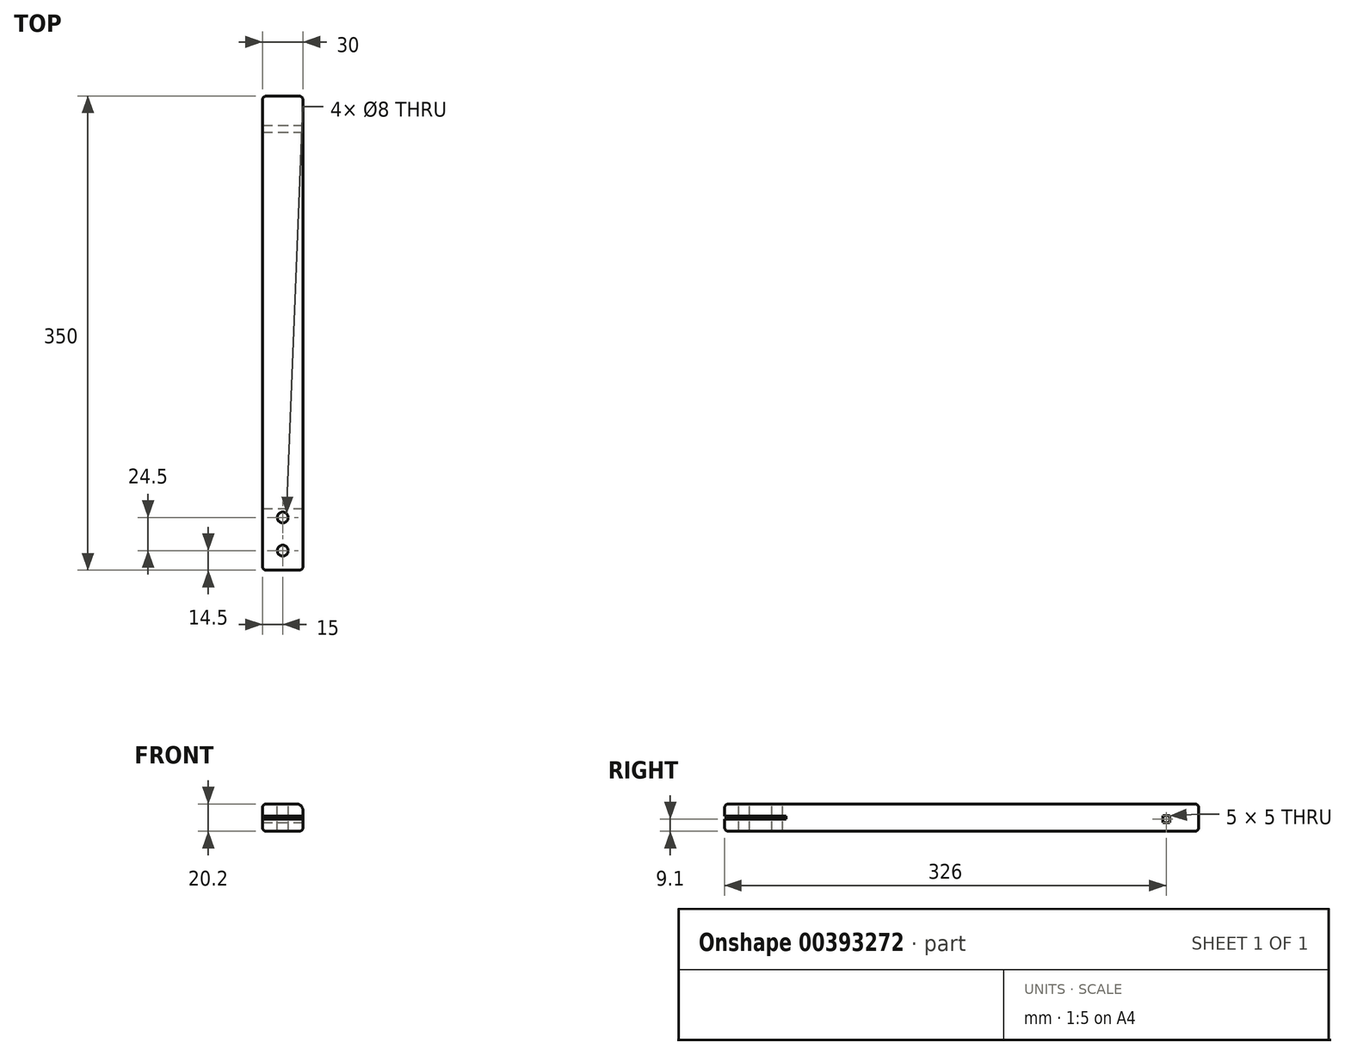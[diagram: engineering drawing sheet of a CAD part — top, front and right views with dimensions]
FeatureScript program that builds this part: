
annotation { "Feature Type Name" : "Feature", "Feature Type Description" : "" }
export const myFeature = defineFeature(function(context is Context, id is Id, definition is map)
    precondition{}
    {
        {
            var Q0;
            Q0=qCreatedBy(makeId("Front.planeOp"),FACE);
            var sketch = newSketch(context, id + "F0", { "sketchPlane" : qUnion([Q0])});
            skLineSegment(sketch, "E0.bottom", {"start": v(-15, -10.1) * mm, "end": v(15, -10.1) * mm});
            skLineSegment(sketch, "E0.top", {"start": v(-15, 10.1) * mm, "end": v(15, 10.1) * mm});
            skLineSegment(sketch, "E0.left", {"start": v(-15, -10.1) * mm, "end": v(-15, 10.1) * mm});
            skLineSegment(sketch, "E0.right", {"start": v(15, -10.1) * mm, "end": v(15, 10.1) * mm});
            skPoint(sketch, "E0.middle", {"position": v(0, 0) * mm});
            skSolve(sketch);
        }
        {
            var Q0;
            Q0 = qSketchRegion(id + "F0", true);
            extrude(context, id + "F1", {"entities" : qUnion([Q0]), "oppositeDirection" : true, "depth" : 350 * mm});
        }
        {
            var Q0;
            Q0=makeQuery(id+"F1.opExtrude","SWEPT_EDGE",EDGE,{"disambiguationData":[OSD([sQuery(id+"F0.wireOp",EDGE,"E0.top"),sQuery(id+"F0.wireOp",EDGE,"E0.right")])]});
            fillet(context, id + "F2", {"entities" : qUnion([Q0]), "radius" : 5 * mm, "tangentPropagation" : true, "allowEdgeOverflow" : false});
        }
        {
            var Q0;
            Q0=makeQuery(id+"F1.opExtrude","SWEPT_EDGE",EDGE,{"disambiguationData":[OSD([sQuery(id+"F0.wireOp",EDGE,"E0.top"),sQuery(id+"F0.wireOp",EDGE,"E0.left")])]});
            var Q1;
            Q1=makeQuery(id+"F1.opExtrude","CAP_EDGE",EDGE,{"disambiguationData":[OSD([sQuery(id+"F0.wireOp",EDGE,"E0.top")])],"isStart":true});
            var Q2;
            Q2=makeQuery(id+"F1.opExtrude","SWEPT_FACE",FACE,{"disambiguationData":[OSD([sQuery(id+"F0.wireOp",EDGE,"E0.bottom")])]});
            var Q3;
            Q3=makeQuery(id+"F1.opExtrude","CAP_EDGE",EDGE,{"disambiguationData":[OSD([sQuery(id+"F0.wireOp",EDGE,"E0.left")])],"isStart":true});
            var Q4;
            Q4=makeQuery(id+"F1.opExtrude","CAP_EDGE",EDGE,{"disambiguationData":[OSD([sQuery(id+"F0.wireOp",EDGE,"E0.top")])],"isStart":false});
            var Q5;
            Q5=makeQuery(id+"F1.opExtrude","CAP_EDGE",EDGE,{"disambiguationData":[OSD([sQuery(id+"F0.wireOp",EDGE,"E0.left")])],"isStart":false});
            fillet(context, id + "F3", {"entities" : qUnion([Q0, Q1, Q2, Q3, Q4, Q5]), "radius" : 3 * mm, "tangentPropagation" : true, "allowEdgeOverflow" : false});
        }
        {
            var Q0;
            Q0=makeQuery(id+"F1.opExtrude","SWEPT_FACE",FACE,{"disambiguationData":[OSD([sQuery(id+"F0.wireOp",EDGE,"E0.right")])]});
            var sketch = newSketch(context, id + "F4", { "sketchPlane" : qUnion([Q0])});
            skLineSegment(sketch, "E1.bottom", {"start": v(0, -1) * mm, "end": v(45.5, -1) * mm});
            skLineSegment(sketch, "E1.top", {"start": v(0, 1) * mm, "end": v(45.5, 1) * mm});
            skLineSegment(sketch, "E1.left", {"start": v(0, -1) * mm, "end": v(0, 1) * mm});
            skLineSegment(sketch, "E1.right", {"start": v(45.5, -1) * mm, "end": v(45.5, 1) * mm});
            skPoint(sketch, "E1.middle", {"position": v(22.75, 0) * mm});
            skSolve(sketch);
        }
        {
            var Q0;
            Q0 = qSketchRegion(id + "F4", true);
            extrude(context, id + "F5", {"entities" : qUnion([Q0]), "operationType" : NewBodyOperationType.REMOVE, "endBound" : BoundingType.THROUGH_ALL, "oppositeDirection" : true, "depth" : 25 * mm});
        }
        {
            var Q0;
            Q0=makeQuery(id+"F1.opExtrude","SWEPT_FACE",FACE,{"disambiguationData":[OSD([sQuery(id+"F0.wireOp",EDGE,"E0.right")])]});
            var sketch = newSketch(context, id + "F6", { "sketchPlane" : qUnion([Q0])});
            skLineSegment(sketch, "E2.bottom", {"start": v(323.5, -3.5) * mm, "end": v(328.5, -3.5) * mm});
            skLineSegment(sketch, "E2.top", {"start": v(323.5, 1.5) * mm, "end": v(328.5, 1.5) * mm});
            skLineSegment(sketch, "E2.left", {"start": v(323.5, -3.5) * mm, "end": v(323.5, 1.5) * mm});
            skLineSegment(sketch, "E2.right", {"start": v(328.5, -3.5) * mm, "end": v(328.5, 1.5) * mm});
            skPoint(sketch, "E2.middle", {"position": v(326, -1) * mm});
            skPoint(sketch, "E2.middle.positionSnap0", {"position": v(347, -1) * mm});
            skPoint(sketch, "E2.centerSnap0", {"position": v(347, -1) * mm});
            skSolve(sketch);
        }
        {
            var Q0;
            Q0 = qSketchRegion(id + "F6", true);
            extrude(context, id + "F7", {"entities" : qUnion([Q0]), "operationType" : NewBodyOperationType.REMOVE, "endBound" : BoundingType.THROUGH_ALL, "oppositeDirection" : true, "depth" : 25 * mm});
        }
        {
            var Q0;
            Q0=makeQuery(id+"F1.opExtrude","SWEPT_FACE",FACE,{"disambiguationData":[OSD([sQuery(id+"F0.wireOp",EDGE,"E0.top")])]});
            var sketch = newSketch(context, id + "F8", { "sketchPlane" : qUnion([Q0])});
            skCircle(sketch, "E3", {"center": v(0, 14.5) * mm, "radius": 4 * mm});
            skCircle(sketch, "E4", {"center": v(0, 39) * mm, "radius": 4 * mm});
            skSolve(sketch);
        }
        {
            var Q0;
            Q0 = qSketchRegion(id + "F8", true);
            extrude(context, id + "F9", {"entities" : qUnion([Q0]), "operationType" : NewBodyOperationType.REMOVE, "endBound" : BoundingType.THROUGH_ALL, "oppositeDirection" : true, "depth" : 25 * mm});
        }
        {
            var Q0;
            Q0 = qSketchRegion(id + "F6", true);
            extrude(context, id + "F10", {"entities" : qUnion([Q0]), "operationType" : NewBodyOperationType.REMOVE, "endBound" : BoundingType.THROUGH_ALL, "oppositeDirection" : true, "depth" : 25 * mm});
        }
    });
